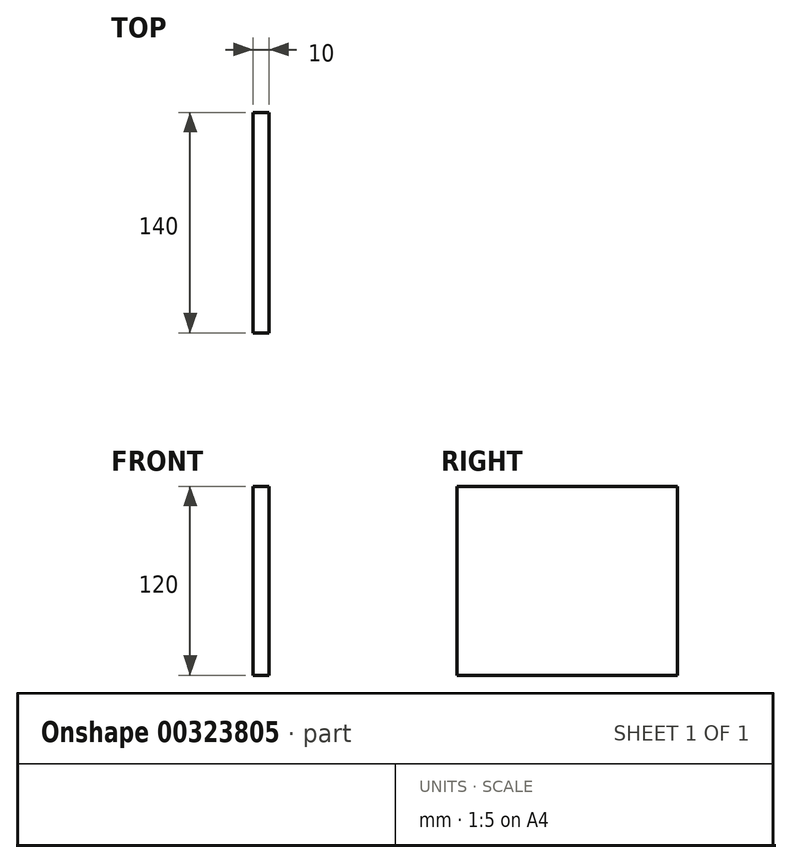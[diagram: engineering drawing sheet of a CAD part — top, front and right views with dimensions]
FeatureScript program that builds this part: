
annotation { "Feature Type Name" : "Feature", "Feature Type Description" : "" }
export const myFeature = defineFeature(function(context is Context, id is Id, definition is map)
    precondition{}
    {
        {
            var Q0;
            Q0=qCreatedBy(makeId("Front.planeOp"),FACE);
            var sketch = newSketch(context, id + "F0", { "sketchPlane" : qUnion([Q0])});
            skLineSegment(sketch, "E0.bottom", {"start": v(-5, 60) * mm, "end": v(5, 60) * mm});
            skLineSegment(sketch, "E0.top", {"start": v(-5, -60) * mm, "end": v(5, -60) * mm});
            skLineSegment(sketch, "E0.left", {"start": v(-5, 60) * mm, "end": v(-5, -60) * mm});
            skLineSegment(sketch, "E0.right", {"start": v(5, 60) * mm, "end": v(5, -60) * mm});
            skPoint(sketch, "E0.middle", {"position": v(0, 0) * mm});
            skSolve(sketch);
        }
        {
            var Q0;
            Q0 = qSketchRegion(id + "F0", true);
            extrude(context, id + "F1", {"entities" : qUnion([Q0]), "depth" : 140 * mm});
        }
    });
